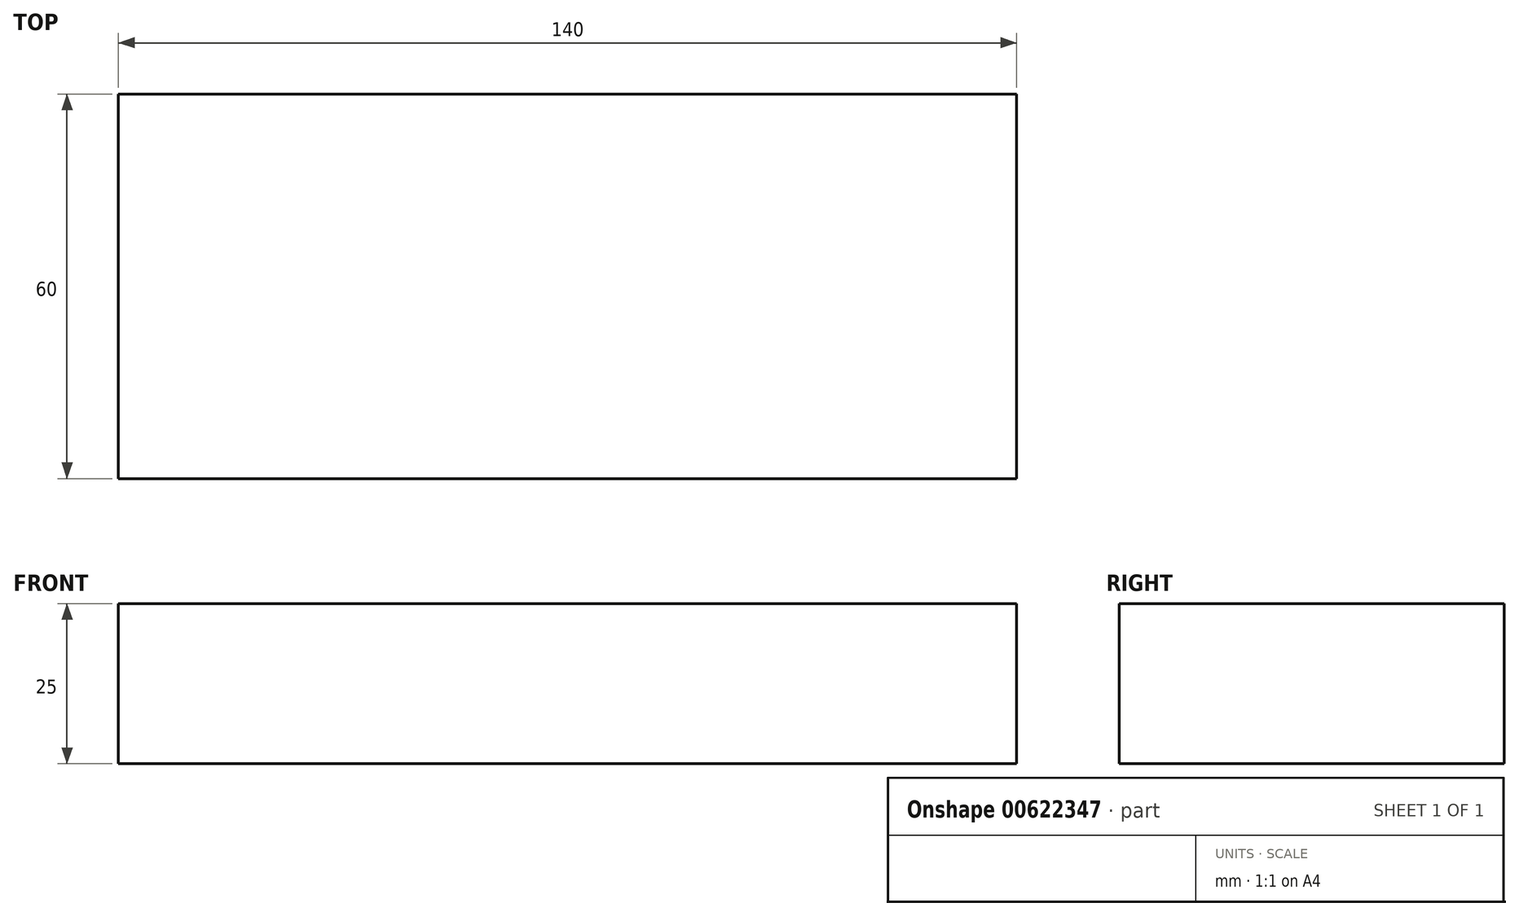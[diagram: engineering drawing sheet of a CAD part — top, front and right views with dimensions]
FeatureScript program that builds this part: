
annotation { "Feature Type Name" : "Feature", "Feature Type Description" : "" }
export const myFeature = defineFeature(function(context is Context, id is Id, definition is map)
    precondition{}
    {
        {
            var Q0;
            Q0=qCreatedBy(makeId("Top.planeOp"),FACE);
            var sketch = newSketch(context, id + "F0", { "sketchPlane" : qUnion([Q0])});
            skLineSegment(sketch, "E0.bottom", {"start": v(70, -30) * mm, "end": v(-70, -30) * mm});
            skLineSegment(sketch, "E0.top", {"start": v(70, 30) * mm, "end": v(-70, 30) * mm});
            skLineSegment(sketch, "E0.left", {"start": v(70, -30) * mm, "end": v(70, 30) * mm});
            skLineSegment(sketch, "E0.right", {"start": v(-70, -30) * mm, "end": v(-70, 30) * mm});
            skPoint(sketch, "E0.middle", {"position": v(0, 0) * mm});
            skSolve(sketch);
        }
        {
            var Q0;
            Q0=makeQuery(id+"F0.imprint","IMPRINT",FACE,{"disambiguationData":[TD([[makeQuery(id+"F0.imprint","IMPRINT",EDGE,{"derivedFrom":sQuery(id+"F0.wireOp",EDGE,"E0.bottom")}),-1.0]])]});
            extrude(context, id + "F1", {"entities" : qUnion([Q0]), "depth" : 25 * mm, "offsetDistance" : 25 * mm});
        }
    });
